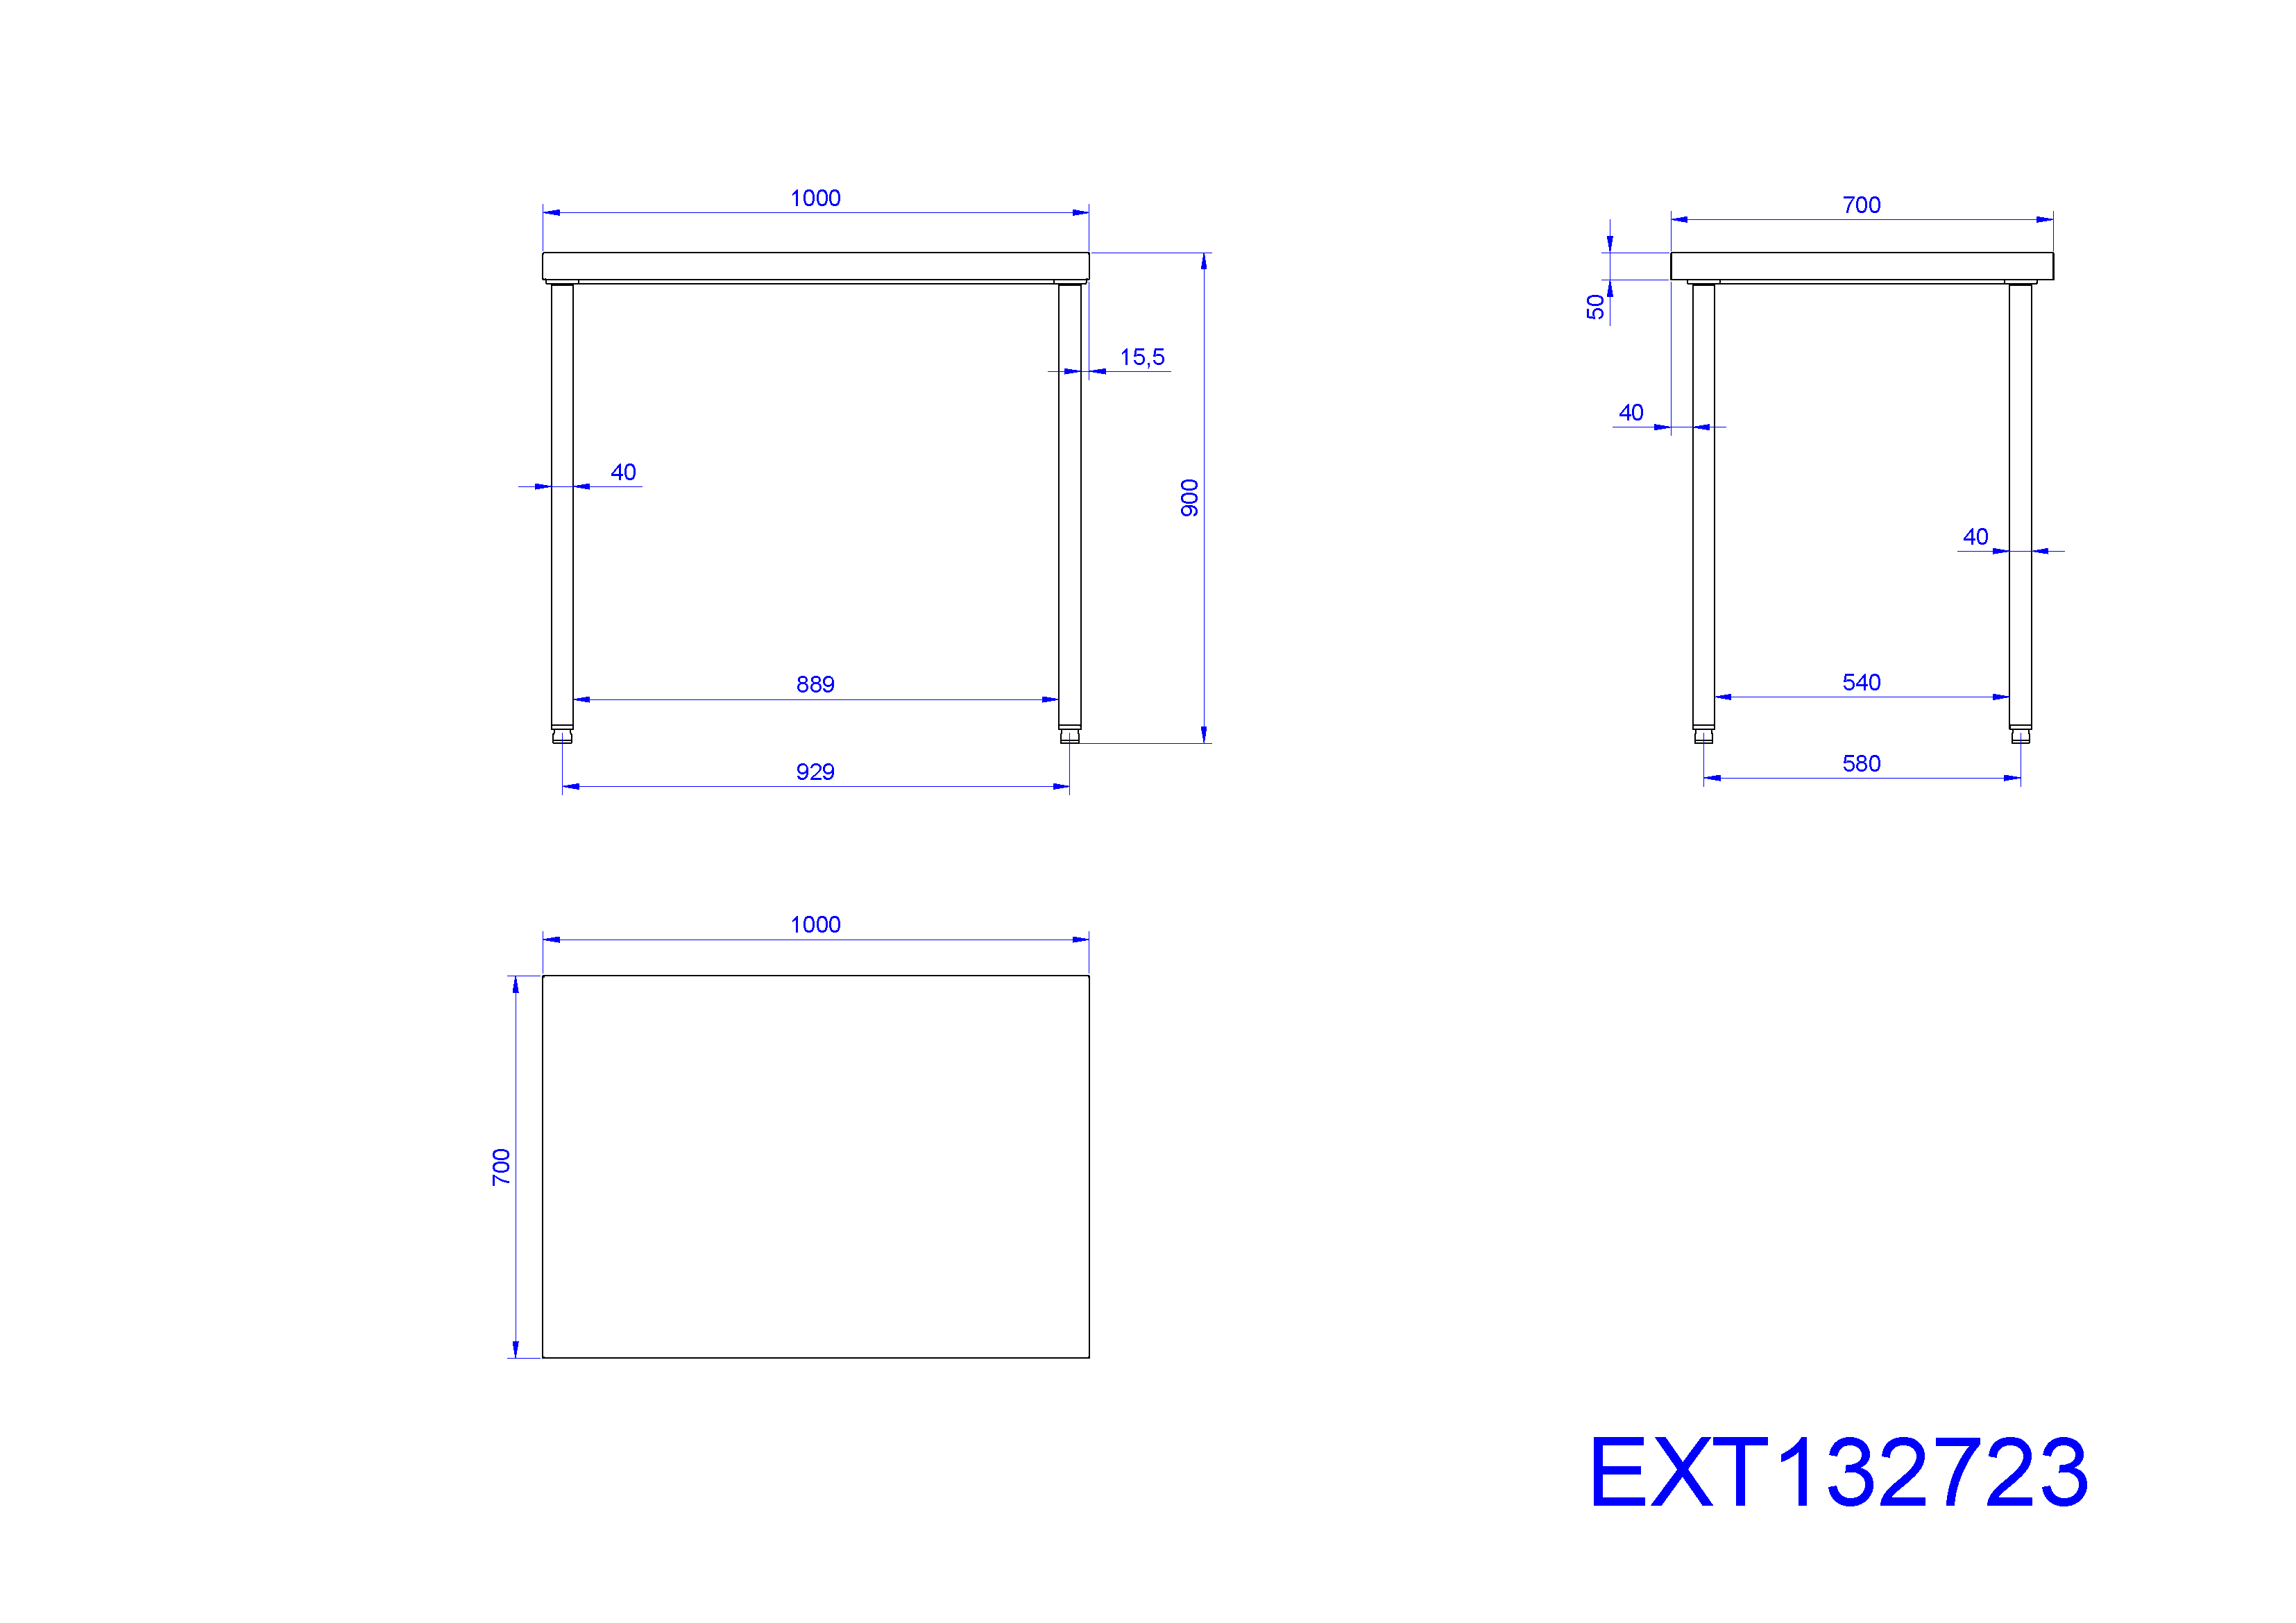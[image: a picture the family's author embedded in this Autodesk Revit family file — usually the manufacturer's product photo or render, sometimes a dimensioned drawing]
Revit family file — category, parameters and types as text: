
# Revit family: QF_ELECTROLUXPROFESSIONAL_132840_WTD1207N
name_source: partatom
category: Attrezzature speciali
units: mm (PartAtom-declared; Revit-internal decimal feet)

## family parameters
Basato su piano di lavoro = No
Condiviso = No
Punto di calcolo locali = No
Quota connettore circolare = Usa diametro
Sempre verticale = Sì
Taglio con vuoti quando caricato = No
Tipo di parte = Normale

## types (1)
- Standard
    Accessory = Sì
    Cold Water Size = 0 mm
    Compressed Air Pressure = 0.0 Pa
    Compressed Air Size = 0 mm
    Compressed Air Volume = 0.0 L/s
    Condensate Return Size = 0 mm
    Cycle = 0 Hz
    Depth Actual = 700 mm  [stored 2.29659 ft]
    Descrizione = WORK TABLE-DISASSEMBLED 1200MM
    Direct Waste Size = 0 mm
    Gas Input Pressure = 0
    Gas KW = 0
    Gas Size = 0 mm
    HP = 0 HP
    Height Actual = 900 mm  [stored 2.95276 ft]
    Hot Water Size = 0 mm
    Item Number = 132840
    Length Actual = 1200 mm
    Modello = WTD1207N
    Phase = 0
    Produttore = Electrolux Professional
    Prospetto di default = 0 mm  [stored 0 ft]
    Refrigerant Compressor Remote = Sì
    Refrigeration Liquid Line Size = 0 mm  [stored 0 ft]
    Refrigeration Suction Line Size = 0 mm  [stored 0 ft]
    Steam Consumption per Hour = 0
    Steam Supply Maximum Pressure = 0.0 Pa
    Steam Supply Minimum Pressure = 0.0 Pa
    Steam Supply Size = 0 mm
    URL = https://www.electroluxprofessional.com
    URL Manufacturer = https://www.electroluxprofessional.com
    Volts = 0 V
    Watts = 0 W
    Weight = 43.00 kg

note: source unit labels omitted for Gas Input Pressure — the stored unit's dimension contradicts the parameter name (converter mislabeling)

note: [stored X ft] marks values corroborated as IEEE doubles in the binary element streams (Revit-internal decimal feet)

## geometry (parser evidence)
native form markers: Sweep x2
no freeform markers — native parametric forms only
